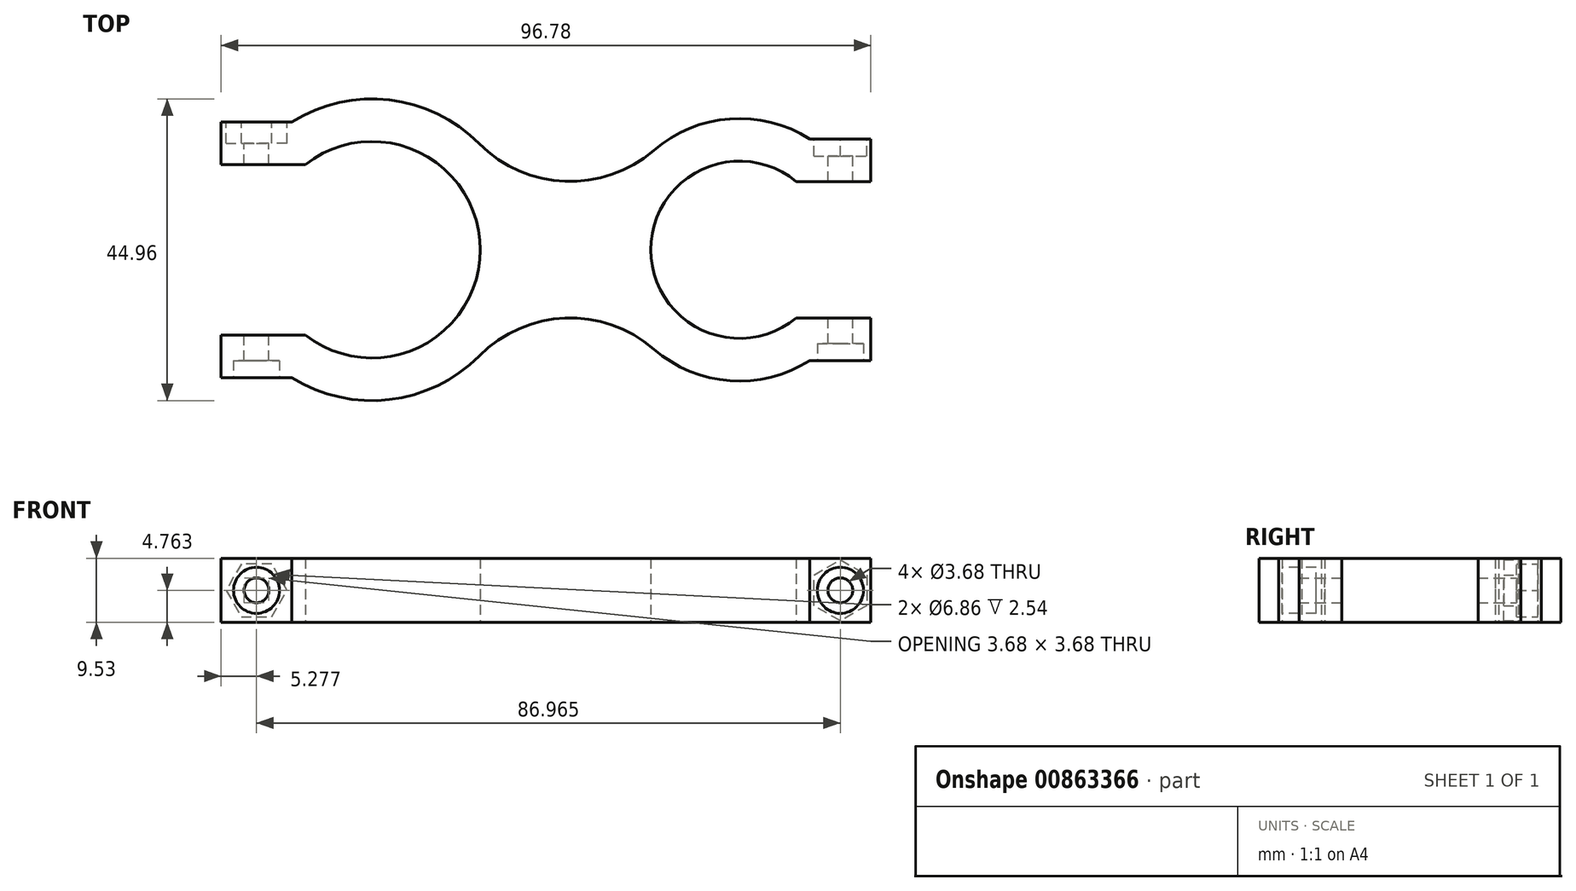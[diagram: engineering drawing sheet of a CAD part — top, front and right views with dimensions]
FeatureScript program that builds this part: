
annotation { "Feature Type Name" : "Feature", "Feature Type Description" : "" }
export const myFeature = defineFeature(function(context is Context, id is Id, definition is map)
    precondition{}
    {
        {
            var Q0;
            Q0=qCreatedBy(makeId("Top.planeOp"),FACE);
            var sketch = newSketch(context, id + "F0", { "sketchPlane" : qUnion([Q0])});
            skCircle(sketch, "E0", {"center": v(0, 0) * mm, "radius": 13.2 * mm});
            skCircle(sketch, "E1", {"center": v(-54.74, 0) * mm, "radius": 16.13 * mm});
            skCircle(sketch, "E2.0", {"center": v(-54.74, 0) * mm, "radius": 22.48 * mm});
            skCircle(sketch, "E3.0", {"center": v(0, 0) * mm, "radius": 19.56 * mm});
            skArc(sketch, "E4", {"start": v(-38.77, 15.82) * mm, "mid": v(-25.97, 10.19) * mm, "end": v(-12.78, 14.8) * mm});
            skLineSegment(sketch, "E5", {"start": v(-64.68, 12.7) * mm, "end": v(-77.22, 12.7) * mm});
            skLineSegment(sketch, "E6", {"start": v(-77.22, 12.7) * mm, "end": v(-77.22, 19.05) * mm});
            skLineSegment(sketch, "E7", {"start": v(-77.22, 19.05) * mm, "end": v(-66.67, 19.05) * mm});
            skLineSegment(sketch, "E8", {"start": v(-77.22, 15.88) * mm, "end": v(-70.65, 15.88) * mm, "construction": true});
            skLineSegment(sketch, "E9", {"start": v(-54.74, 0) * mm, "end": v(0, 0) * mm, "construction": true});
            skLineSegment(sketch, "E10", {"start": v(8.44, 10.16) * mm, "end": v(19.56, 10.16) * mm});
            skLineSegment(sketch, "E11", {"start": v(19.56, 10.16) * mm, "end": v(19.56, 16.51) * mm});
            skLineSegment(sketch, "E12", {"start": v(19.56, 16.51) * mm, "end": v(10.49, 16.51) * mm});
            skArc(sketch, "E13.MirrorCS", {"start": v(-38.77, -15.82) * mm, "mid": v(-25.97, -10.19) * mm, "end": v(-12.78, -14.8) * mm});
            skLineSegment(sketch, "E14.MirrorCS", {"start": v(8.44, -10.16) * mm, "end": v(19.56, -10.16) * mm});
            skLineSegment(sketch, "E15.MirrorCS", {"start": v(19.56, -10.16) * mm, "end": v(19.56, -16.51) * mm});
            skLineSegment(sketch, "E16.MirrorCS", {"start": v(19.56, -16.51) * mm, "end": v(10.49, -16.51) * mm});
            skLineSegment(sketch, "E17.MirrorCS", {"start": v(-64.68, -12.7) * mm, "end": v(-77.22, -12.7) * mm});
            skLineSegment(sketch, "E18.MirrorCS", {"start": v(-77.22, -19.05) * mm, "end": v(-66.67, -19.05) * mm});
            skLineSegment(sketch, "E19.MirrorCS", {"start": v(-77.22, -12.7) * mm, "end": v(-77.22, -19.05) * mm});
            skSolve(sketch);
        }
        {
            var Q0;
            {var subQ5=sQuery(id+"F0.wireOp",EDGE,"E5");var subQ8=sQuery(id+"F0.wireOp",EDGE,"E1");var subQ9=makeQuery(id+"F0.imprint","INTERSECT",VERTEX,{"derivedFrom":[subQ8,subQ5]});Q0=makeQuery(id+"F0.imprint","IMPRINT",FACE,{"disambiguationData":[TD([[makeQuery(id+"F0.imprint","IMPRINT",EDGE,{"disambiguationData":[TD([[subQ9,1.0]])],"derivedFrom":subQ8}),-1.0]])]});}
            var Q1;
            {var subQ4=sQuery(id+"F0.wireOp",EDGE,"E6");Q1=makeQuery(id+"F0.imprint","IMPRINT",FACE,{"disambiguationData":[TD([[makeQuery(id+"F0.imprint","IMPRINT",EDGE,{"derivedFrom":subQ4}),-1.0]])]});}
            var Q2;
            {var subQ0=sQuery(id+"F0.wireOp",EDGE,"E18.MirrorCS");Q2=makeQuery(id+"F0.imprint","IMPRINT",FACE,{"disambiguationData":[TD([[makeQuery(id+"F0.imprint","IMPRINT",EDGE,{"derivedFrom":subQ0}),1.0]])]});}
            var Q3;
            {var subQ0=sQuery(id+"F0.wireOp",EDGE,"E4");Q3=makeQuery(id+"F0.imprint","IMPRINT",FACE,{"disambiguationData":[TD([[makeQuery(id+"F0.imprint","IMPRINT",EDGE,{"derivedFrom":subQ0}),-1.0]])]});}
            var Q4;
            {var subQ4=sQuery(id+"F0.wireOp",EDGE,"E10");var subQ5=sQuery(id+"F0.wireOp",EDGE,"E0");var subQ6=makeQuery(id+"F0.imprint","INTERSECT",VERTEX,{"derivedFrom":[subQ5,subQ4]});Q4=makeQuery(id+"F0.imprint","IMPRINT",FACE,{"disambiguationData":[TD([[makeQuery(id+"F0.imprint","IMPRINT",EDGE,{"disambiguationData":[TD([[subQ6,-1.0]])],"derivedFrom":subQ5}),-1.0]])]});}
            var Q5;
            {var subQ4=sQuery(id+"F0.wireOp",EDGE,"E15.MirrorCS");Q5=makeQuery(id+"F0.imprint","IMPRINT",FACE,{"disambiguationData":[TD([[makeQuery(id+"F0.imprint","IMPRINT",EDGE,{"derivedFrom":subQ4}),-1.0]])]});}
            var Q6;
            {var subQ4=sQuery(id+"F0.wireOp",EDGE,"E11");Q6=makeQuery(id+"F0.imprint","IMPRINT",FACE,{"disambiguationData":[TD([[makeQuery(id+"F0.imprint","IMPRINT",EDGE,{"derivedFrom":subQ4}),1.0]])]});}
            extrude(context, id + "F1", {"entities" : qUnion([Q0, Q1, Q2, Q3, Q4, Q5, Q6]), "depth" : 9.52 * mm, "offsetDistance" : 25.4 * mm});
        }
        {
            var Q0;
            Q0=makeQuery(id+"F1.opExtrude","SWEPT_FACE",FACE,{"disambiguationData":[OSD([sQuery(id+"F0.wireOp",EDGE,"E7")])]});
            var sketch = newSketch(context, id + "F2", { "sketchPlane" : qUnion([Q0])});
            skLineSegment(sketch, "E20.0.0", {"start": v(-19.56, 0) * mm, "end": v(-10.49, 0) * mm});
            skLineSegment(sketch, "E20.0.1", {"start": v(-10.49, 0) * mm, "end": v(-10.49, 9.53) * mm});
            skLineSegment(sketch, "E20.0.2", {"start": v(-10.49, 9.53) * mm, "end": v(-19.56, 9.53) * mm});
            skLineSegment(sketch, "E20.0.3", {"start": v(-19.56, 9.53) * mm, "end": v(-19.56, 0) * mm});
            skLineSegment(sketch, "E21.0.0", {"start": v(66.67, 0) * mm, "end": v(77.22, 0) * mm});
            skLineSegment(sketch, "E21.0.1", {"start": v(77.22, 0) * mm, "end": v(77.22, 9.53) * mm});
            skLineSegment(sketch, "E21.0.2", {"start": v(77.22, 9.53) * mm, "end": v(66.67, 9.53) * mm});
            skLineSegment(sketch, "E21.0.3", {"start": v(66.67, 9.53) * mm, "end": v(66.67, 0) * mm});
            skCircle(sketch, "E22", {"center": v(71.94, 4.76) * mm, "radius": 1.84 * mm});
            skPoint(sketch, "E22.centerSnap0", {"position": v(71.94, 0) * mm});
            skPoint(sketch, "E22.centerSnap1", {"position": v(77.22, 4.76) * mm});
            skCircle(sketch, "E23", {"center": v(-15.02, 4.76) * mm, "radius": 1.84 * mm});
            skPoint(sketch, "E23.centerSnap0", {"position": v(-19.56, 4.76) * mm});
            skPoint(sketch, "E23.centerSnap1", {"position": v(-15.02, 0) * mm});
            skCircle(sketch, "E24.cCircle", {"center": v(71.94, 4.76) * mm, "radius": 3.94 * mm, "construction": true});
            skLineSegment(sketch, "E24.0", {"start": v(67.4, 4.76) * mm, "end": v(69.67, 8.7) * mm});
            skLineSegment(sketch, "E24.1", {"start": v(69.67, 8.7) * mm, "end": v(74.22, 8.7) * mm});
            skLineSegment(sketch, "E24.2", {"start": v(74.22, 8.7) * mm, "end": v(76.49, 4.76) * mm});
            skLineSegment(sketch, "E24.3", {"start": v(76.49, 4.76) * mm, "end": v(74.22, 0.83) * mm});
            skLineSegment(sketch, "E24.4", {"start": v(74.22, 0.83) * mm, "end": v(69.67, 0.83) * mm});
            skLineSegment(sketch, "E24.5", {"start": v(69.67, 0.83) * mm, "end": v(67.4, 4.76) * mm});
            skPoint(sketch, "E24.0.midPoint", {"position": v(68.53, 6.73) * mm});
            skCircle(sketch, "E25.cCircle", {"center": v(-15.02, 4.76) * mm, "radius": 3.94 * mm, "construction": true});
            skLineSegment(sketch, "E25.0", {"start": v(-18.96, 2.49) * mm, "end": v(-18.96, 7.04) * mm});
            skLineSegment(sketch, "E25.1", {"start": v(-18.96, 7.04) * mm, "end": v(-15.02, 9.3) * mm});
            skLineSegment(sketch, "E25.2", {"start": v(-15.02, 9.3) * mm, "end": v(-11.08, 7.04) * mm});
            skLineSegment(sketch, "E25.3", {"start": v(-11.08, 7.04) * mm, "end": v(-11.08, 2.49) * mm});
            skLineSegment(sketch, "E25.4", {"start": v(-11.08, 2.49) * mm, "end": v(-15.02, 0.22) * mm});
            skLineSegment(sketch, "E25.5", {"start": v(-15.02, 0.22) * mm, "end": v(-18.96, 2.49) * mm});
            skPoint(sketch, "E25.0.midPoint", {"position": v(-18.96, 4.76) * mm});
            skSolve(sketch);
        }
        {
            var Q0;
            Q0=makeQuery(id+"F2.imprint","IMPRINT",FACE,{"disambiguationData":[TD([[makeQuery(id+"F2.imprint","IMPRINT",EDGE,{"derivedFrom":sQuery(id+"F2.wireOp",EDGE,"E22")}),1.0]])]});
            var Q1;
            Q1=makeQuery(id+"F2.imprint","IMPRINT",FACE,{"disambiguationData":[TD([[makeQuery(id+"F2.imprint","IMPRINT",EDGE,{"derivedFrom":sQuery(id+"F2.wireOp",EDGE,"E23")}),1.0]])]});
            extrude(context, id + "F3", {"entities" : qUnion([Q0, Q1]), "operationType" : NewBodyOperationType.REMOVE, "endBound" : BoundingType.THROUGH_ALL, "oppositeDirection" : true, "depth" : 25.4 * mm, "offsetDistance" : 25.4 * mm});
        }
        {
            var Q0;
            Q0=makeQuery(id+"F2.imprint","IMPRINT",FACE,{"disambiguationData":[TD([[makeQuery(id+"F2.imprint","IMPRINT",EDGE,{"derivedFrom":sQuery(id+"F2.wireOp",EDGE,"E22")}),-1.0]])]});
            extrude(context, id + "F4", {"entities" : qUnion([Q0]), "operationType" : NewBodyOperationType.REMOVE, "oppositeDirection" : true, "depth" : 3.17 * mm, "offsetDistance" : 25.4 * mm});
        }
        {
            var Q0;
            Q0=makeQuery(id+"F2.imprint","IMPRINT",FACE,{"disambiguationData":[TD([[makeQuery(id+"F2.imprint","IMPRINT",EDGE,{"derivedFrom":sQuery(id+"F2.wireOp",EDGE,"E23")}),-1.0]])]});
            extrude(context, id + "F5", {"entities" : qUnion([Q0]), "operationType" : NewBodyOperationType.REMOVE, "oppositeDirection" : true, "depth" : 5.08 * mm, "offsetDistance" : 25.4 * mm});
        }
        {
            var Q0;
            Q0=makeQuery(id+"F1.opExtrude","SWEPT_FACE",FACE,{"disambiguationData":[OSD([sQuery(id+"F0.wireOp",EDGE,"E16.MirrorCS")])]});
            var sketch = newSketch(context, id + "F6", { "sketchPlane" : qUnion([Q0])});
            skCircle(sketch, "E26", {"center": v(15.02, 4.76) * mm, "radius": 3.43 * mm});
            skSolve(sketch);
        }
        {
            var Q0;
            Q0=makeQuery(id+"F6.imprint","IMPRINT",FACE,{"disambiguationData":[TD([[makeQuery(id+"F6.imprint","IMPRINT",EDGE,{"derivedFrom":sQuery(id+"F6.wireOp",EDGE,"E26")}),1.0]])]});
            extrude(context, id + "F7", {"entities" : qUnion([Q0]), "operationType" : NewBodyOperationType.REMOVE, "oppositeDirection" : true, "depth" : 2.54 * mm, "offsetDistance" : 25.4 * mm});
        }
        {
            var Q0;
            Q0=makeQuery(id+"F1.opExtrude","SWEPT_FACE",FACE,{"disambiguationData":[OSD([sQuery(id+"F0.wireOp",EDGE,"E18.MirrorCS")])]});
            var sketch = newSketch(context, id + "F8", { "sketchPlane" : qUnion([Q0])});
            skCircle(sketch, "E27", {"center": v(-71.94, 4.76) * mm, "radius": 3.43 * mm});
            skSolve(sketch);
        }
        {
            var Q0;
            Q0=makeQuery(id+"F8.imprint","IMPRINT",FACE,{"disambiguationData":[TD([[makeQuery(id+"F8.imprint","IMPRINT",EDGE,{"derivedFrom":sQuery(id+"F8.wireOp",EDGE,"E27")}),1.0]])]});
            extrude(context, id + "F9", {"entities" : qUnion([Q0]), "operationType" : NewBodyOperationType.REMOVE, "oppositeDirection" : true, "depth" : 2.54 * mm, "offsetDistance" : 25.4 * mm});
        }
    });
